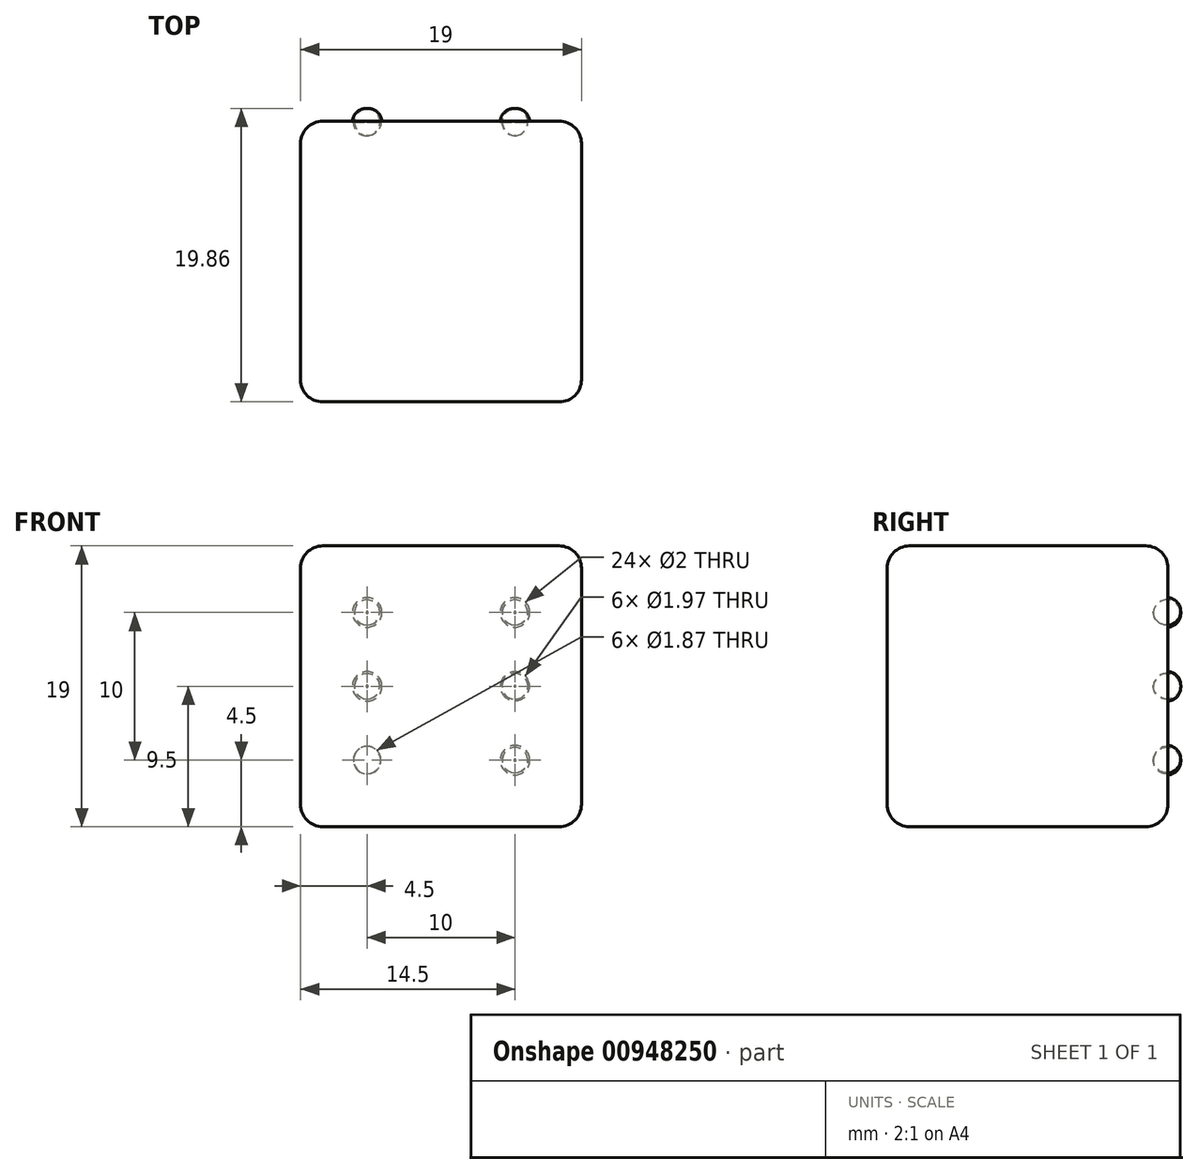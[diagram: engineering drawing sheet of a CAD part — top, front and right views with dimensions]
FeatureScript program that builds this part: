
annotation { "Feature Type Name" : "Feature", "Feature Type Description" : "" }
export const myFeature = defineFeature(function(context is Context, id is Id, definition is map)
    precondition{}
    {
        {
            var Q0;
            Q0=qCreatedBy(makeId("Front.planeOp"),FACE);
            var sketch = newSketch(context, id + "F0", { "sketchPlane" : qUnion([Q0])});
            skLineSegment(sketch, "E0", {"start": v(0, 0) * mm, "end": v(0, 19) * mm});
            skLineSegment(sketch, "E1", {"start": v(0, 19) * mm, "end": v(19, 19) * mm});
            skLineSegment(sketch, "E2", {"start": v(19, 19) * mm, "end": v(19, 0) * mm});
            skLineSegment(sketch, "E3", {"start": v(19, 0) * mm, "end": v(0, 0) * mm});
            skSolve(sketch);
        }
        {
            var Q0;
            Q0=makeQuery(id+"F0.imprint","IMPRINT",FACE,{"disambiguationData":[TD([[makeQuery(id+"F0.imprint","IMPRINT",EDGE,{"derivedFrom":sQuery(id+"F0.wireOp",EDGE,"E0")}),-1.0]])]});
            extrude(context, id + "F1", {"entities" : qUnion([Q0]), "depth" : 19 * mm, "offsetDistance" : 25 * mm});
        }
        {
            var Q0;
            Q0=makeQuery(id+"F1.opExtrude","SWEPT_FACE",FACE,{"disambiguationData":[OSD([sQuery(id+"F0.wireOp",EDGE,"E1")])]});
            var Q1;
            Q1=makeQuery(id+"F1.opExtrude","SWEPT_FACE",FACE,{"disambiguationData":[OSD([sQuery(id+"F0.wireOp",EDGE,"E2")])]});
            var Q2;
            Q2=makeQuery(id+"F1.opExtrude","CAP_FACE",FACE,{"disambiguationData":[OSD([sQuery(id+"F0.wireOp",EDGE,"E0"),sQuery(id+"F0.wireOp",EDGE,"E1"),sQuery(id+"F0.wireOp",EDGE,"E2"),sQuery(id+"F0.wireOp",EDGE,"E3")])],"isStart":true});
            var Q3;
            Q3=makeQuery(id+"F1.opExtrude","CAP_FACE",FACE,{"disambiguationData":[OSD([sQuery(id+"F0.wireOp",EDGE,"E0"),sQuery(id+"F0.wireOp",EDGE,"E1"),sQuery(id+"F0.wireOp",EDGE,"E2"),sQuery(id+"F0.wireOp",EDGE,"E3")])],"isStart":false});
            var Q4;
            Q4=makeQuery(id+"F1.opExtrude","SWEPT_FACE",FACE,{"disambiguationData":[OSD([sQuery(id+"F0.wireOp",EDGE,"E3")])]});
            fillet(context, id + "F2", {"entities" : qUnion([Q0, Q1, Q2, Q3, Q4]), "radius" : 1.5 * mm, "tangentPropagation" : true, "allowEdgeOverflow" : false});
        }
        {
            var Q0;
            Q0=makeQuery(id+"F1.opExtrude","CAP_FACE",FACE,{"disambiguationData":[OSD([sQuery(id+"F0.wireOp",EDGE,"E0"),sQuery(id+"F0.wireOp",EDGE,"E1"),sQuery(id+"F0.wireOp",EDGE,"E2"),sQuery(id+"F0.wireOp",EDGE,"E3")])],"isStart":true});
            var sketch = newSketch(context, id + "F3", { "sketchPlane" : qUnion([Q0])});
            skLineSegment(sketch, "E4", {"start": v(-17.5, 17.5) * mm, "end": v(-17.5, 14.5) * mm});
            skLineSegment(sketch, "E5", {"start": v(-17.5, 1.5) * mm, "end": v(-17.5, 9.5) * mm});
            skLineSegment(sketch, "E6", {"start": v(-17.5, 1.5) * mm, "end": v(-17.5, 4.5) * mm});
            skLineSegment(sketch, "E7", {"start": v(-17.5, 1.5) * mm, "end": v(-14.5, 1.5) * mm});
            skLineSegment(sketch, "E8", {"start": v(-1.5, 17.5) * mm, "end": v(-4.5, 17.5) * mm});
            skCircle(sketch, "E9", {"center": v(-14.5, 14.5) * mm, "radius": 1 * mm});
            skCircle(sketch, "E10", {"center": v(-14.5, 9.5) * mm, "radius": 0.98 * mm});
            skCircle(sketch, "E11", {"center": v(-14.5, 4.5) * mm, "radius": 1 * mm});
            skCircle(sketch, "E12", {"center": v(-4.5, 4.5) * mm, "radius": 0.93 * mm});
            skCircle(sketch, "E13", {"center": v(-4.5, 14.5) * mm, "radius": 1 * mm});
            skCircle(sketch, "E14", {"center": v(-4.5, 9.5) * mm, "radius": 1 * mm});
            skSolve(sketch);
        }
        {
            var Q0;
            Q0=makeQuery(id+"F3.imprint","IMPRINT",FACE,{"disambiguationData":[TD([[makeQuery(id+"F3.imprint","IMPRINT",EDGE,{"derivedFrom":sQuery(id+"F3.wireOp",EDGE,"E10")}),1.0]])]});
            var Q1;
            Q1=makeQuery(id+"F3.imprint","IMPRINT",FACE,{"disambiguationData":[TD([[makeQuery(id+"F3.imprint","IMPRINT",EDGE,{"derivedFrom":sQuery(id+"F3.wireOp",EDGE,"E9")}),1.0]])]});
            var Q2;
            Q2=makeQuery(id+"F3.imprint","IMPRINT",FACE,{"disambiguationData":[TD([[makeQuery(id+"F3.imprint","IMPRINT",EDGE,{"derivedFrom":sQuery(id+"F3.wireOp",EDGE,"E11")}),1.0]])]});
            var Q3;
            Q3=makeQuery(id+"F3.imprint","IMPRINT",FACE,{"disambiguationData":[TD([[makeQuery(id+"F3.imprint","IMPRINT",EDGE,{"derivedFrom":sQuery(id+"F3.wireOp",EDGE,"E12")}),1.0]])]});
            var Q4;
            Q4=makeQuery(id+"F3.imprint","IMPRINT",FACE,{"disambiguationData":[TD([[makeQuery(id+"F3.imprint","IMPRINT",EDGE,{"derivedFrom":sQuery(id+"F3.wireOp",EDGE,"E14")}),1.0]])]});
            var Q5;
            Q5=makeQuery(id+"F3.imprint","IMPRINT",FACE,{"disambiguationData":[TD([[makeQuery(id+"F3.imprint","IMPRINT",EDGE,{"derivedFrom":sQuery(id+"F3.wireOp",EDGE,"E13")}),1.0]])]});
            extrude(context, id + "F4", {"entities" : qUnion([Q0, Q1, Q2, Q3, Q4, Q5]), "operationType" : NewBodyOperationType.REMOVE, "oppositeDirection" : true, "depth" : 1 * mm, "offsetDistance" : 25 * mm});
        }
        {
            var Q0;
            Q0=makeQuery(id+"F4.boolean.opBoolean","COPY",EDGE,{"derivedFrom":makeQuery(id+"F4.opExtrude","CAP_EDGE",EDGE,{"disambiguationData":[OSD([sQuery(id+"F3.wireOp",EDGE,"E9")])],"isStart":false})});
            var Q1;
            Q1=makeQuery(id+"F4.boolean.opBoolean","COPY",EDGE,{"derivedFrom":makeQuery(id+"F4.opExtrude","CAP_EDGE",EDGE,{"disambiguationData":[OSD([sQuery(id+"F3.wireOp",EDGE,"E10")])],"isStart":false})});
            var Q2;
            Q2=makeQuery(id+"F4.boolean.opBoolean","COPY",EDGE,{"derivedFrom":makeQuery(id+"F4.opExtrude","CAP_EDGE",EDGE,{"disambiguationData":[OSD([sQuery(id+"F3.wireOp",EDGE,"E11")])],"isStart":false})});
            var Q3;
            Q3=makeQuery(id+"F4.boolean.opBoolean","COPY",EDGE,{"derivedFrom":makeQuery(id+"F4.opExtrude","CAP_EDGE",EDGE,{"disambiguationData":[OSD([sQuery(id+"F3.wireOp",EDGE,"E12")])],"isStart":false})});
            var Q4;
            Q4=makeQuery(id+"F4.boolean.opBoolean","COPY",EDGE,{"derivedFrom":makeQuery(id+"F4.opExtrude","CAP_EDGE",EDGE,{"disambiguationData":[OSD([sQuery(id+"F3.wireOp",EDGE,"E14")])],"isStart":false})});
            var Q5;
            Q5=makeQuery(id+"F4.boolean.opBoolean","COPY",EDGE,{"derivedFrom":makeQuery(id+"F4.opExtrude","CAP_EDGE",EDGE,{"disambiguationData":[OSD([sQuery(id+"F3.wireOp",EDGE,"E13")])],"isStart":false})});
            fillet(context, id + "F5", {"entities" : qUnion([Q0, Q1, Q2, Q3, Q4, Q5]), "radius" : 0.93 * mm, "tangentPropagation" : true, "allowEdgeOverflow" : false});
        }
    });
